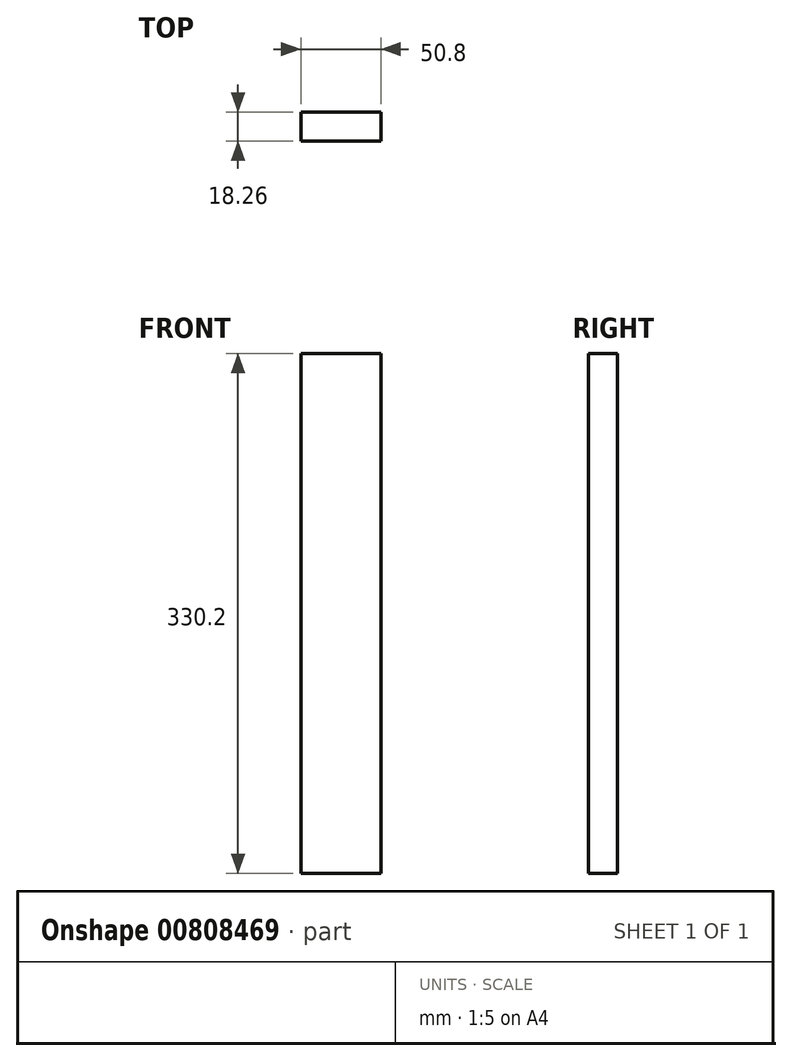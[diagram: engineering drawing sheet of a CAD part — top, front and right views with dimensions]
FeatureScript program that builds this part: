
annotation { "Feature Type Name" : "Feature", "Feature Type Description" : "" }
export const myFeature = defineFeature(function(context is Context, id is Id, definition is map)
    precondition{}
    {
        {
            var Q0;
            Q0=qCreatedBy(makeId("Front.planeOp"),FACE);
            var sketch = newSketch(context, id + "F0", { "sketchPlane" : qUnion([Q0])});
            skLineSegment(sketch, "E0.bottom", {"start": v(25.4, 165.1) * mm, "end": v(-25.4, 165.1) * mm});
            skLineSegment(sketch, "E0.top", {"start": v(25.4, -165.1) * mm, "end": v(-25.4, -165.1) * mm});
            skLineSegment(sketch, "E0.left", {"start": v(25.4, 165.1) * mm, "end": v(25.4, -165.1) * mm});
            skLineSegment(sketch, "E0.right", {"start": v(-25.4, 165.1) * mm, "end": v(-25.4, -165.1) * mm});
            skPoint(sketch, "E0.middle", {"position": v(0, 0) * mm});
            skSolve(sketch);
        }
        {
            var Q0;
            Q0 = qSketchRegion(id + "F0", true);
            extrude(context, id + "F1", {"entities" : qUnion([Q0]), "depth" : 18.26 * mm, "offsetDistance" : 25.4 * mm});
        }
    });
